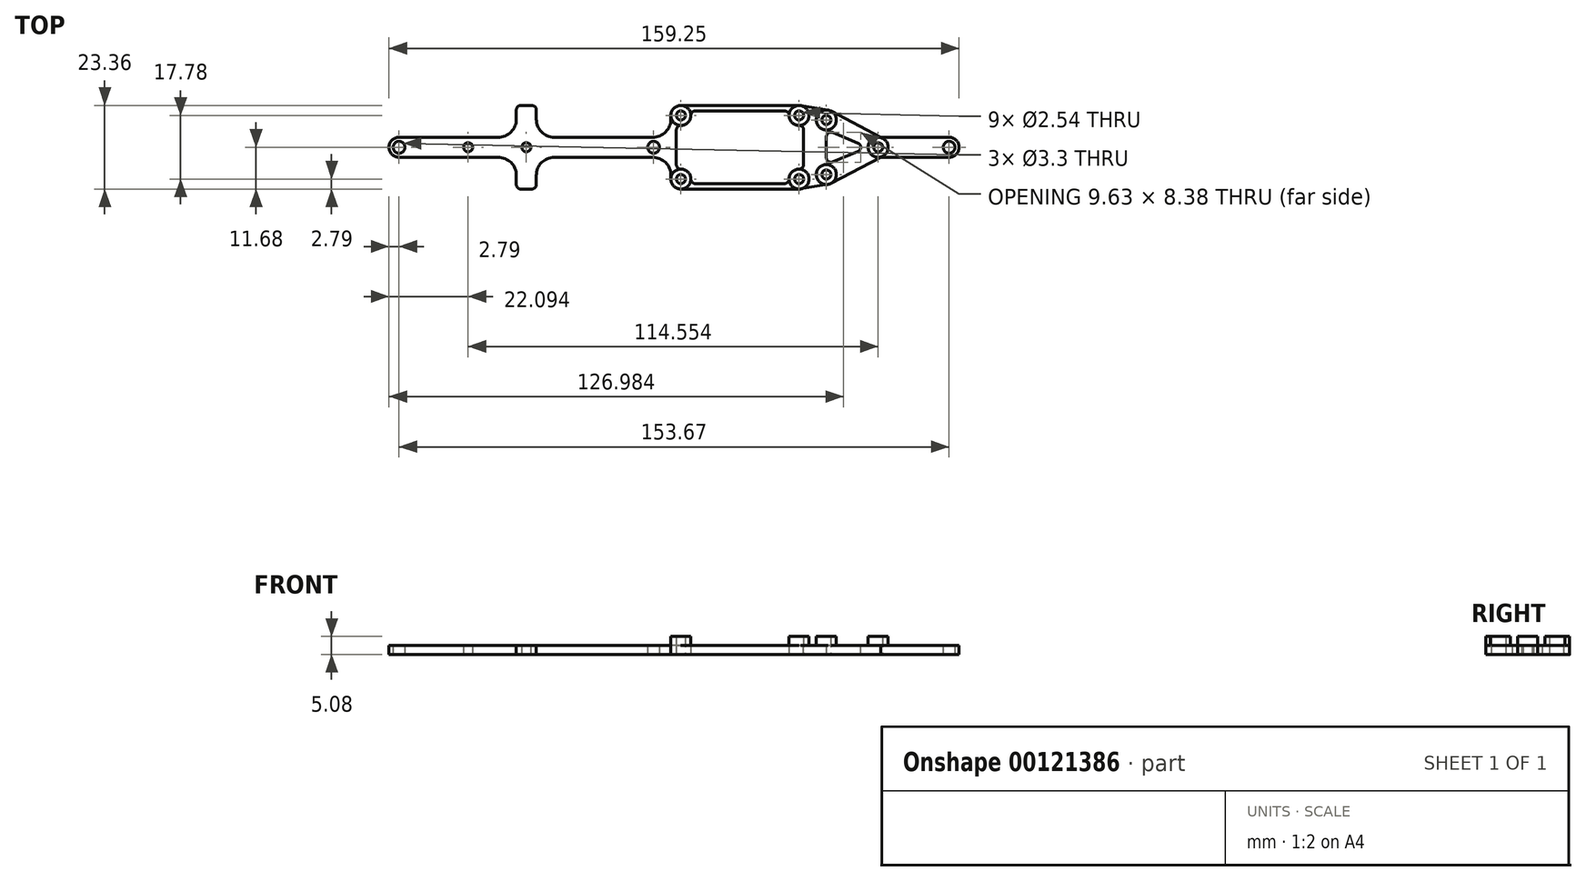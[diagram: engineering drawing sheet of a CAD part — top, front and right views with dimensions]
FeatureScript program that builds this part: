
annotation { "Feature Type Name" : "Feature", "Feature Type Description" : "" }
export const myFeature = defineFeature(function(context is Context, id is Id, definition is map)
    precondition{}
    {
        {
            var Q0;
            Q0=qCreatedBy(makeId("Top.planeOp"),FACE);
            var sketch = newSketch(context, id + "F0", { "sketchPlane" : qUnion([Q0])});
            skCircle(sketch, "E0", {"center": v(-16.51, 8.89) * mm, "radius": 1.27 * mm});
            skCircle(sketch, "E1", {"center": v(-16.51, -8.89) * mm, "radius": 1.27 * mm});
            skCircle(sketch, "E2", {"center": v(16.51, -8.89) * mm, "radius": 1.27 * mm});
            skCircle(sketch, "E3", {"center": v(16.51, 8.89) * mm, "radius": 1.27 * mm});
            skLineSegment(sketch, "E4", {"start": v(-16.51, 8.89) * mm, "end": v(16.51, 8.9) * mm, "construction": true});
            skLineSegment(sketch, "E5", {"start": v(-16.51, 8.89) * mm, "end": v(-16.51, -8.89) * mm, "construction": true});
            skPoint(sketch, "E6", {"position": v(0, 8.9) * mm});
            skPoint(sketch, "E7", {"position": v(-16.51, 0) * mm});
            skCircle(sketch, "E8", {"center": v(24.13, -7.62) * mm, "radius": 1.27 * mm});
            skCircle(sketch, "E9", {"center": v(24.13, 7.62) * mm, "radius": 1.27 * mm});
            skCircle(sketch, "E10", {"center": v(38.6, 0) * mm, "radius": 1.27 * mm});
            skLineSegment(sketch, "E11", {"start": v(25.4, 7.62) * mm, "end": v(25.4, -7.62) * mm, "construction": true});
            skPoint(sketch, "E12", {"position": v(25.4, 0) * mm});
            skCircle(sketch, "E13", {"center": v(-59.69, 0) * mm, "radius": 1.27 * mm});
            skCircle(sketch, "E14", {"center": v(-24.13, 0) * mm, "radius": 1.27 * mm});
            skCircle(sketch, "E15", {"center": v(-95.25, 0) * mm, "radius": 1.65 * mm});
            skCircle(sketch, "E16", {"center": v(58.42, 0) * mm, "radius": 1.65 * mm});
            skCircle(sketch, "E17", {"center": v(-75.95, 0) * mm, "radius": 1.27 * mm});
            skSolve(sketch);
        }
        {
            var Q0;
            Q0=qCreatedBy(makeId("Top.planeOp"),FACE);
            var sketch = newSketch(context, id + "F1", { "sketchPlane" : qUnion([Q0])});
            skCircle(sketch, "E18", {"center": v(-16.51, 8.89) * mm, "radius": 2.8 * mm, "construction": true});
            skCircle(sketch, "E19", {"center": v(-16.51, -8.89) * mm, "radius": 2.8 * mm, "construction": true});
            skCircle(sketch, "E20", {"center": v(16.51, -8.89) * mm, "radius": 2.8 * mm, "construction": true});
            skCircle(sketch, "E21", {"center": v(16.51, 8.9) * mm, "radius": 2.8 * mm, "construction": true});
            skLineSegment(sketch, "E22", {"start": v(-19.3, 8.9) * mm, "end": v(-19.3, 2.8) * mm});
            skLineSegment(sketch, "E23", {"start": v(-16.51, 11.68) * mm, "end": v(16.51, 11.68) * mm});
            skArc(sketch, "E24", {"start": v(-16.51, 11.68) * mm, "mid": v(-18.49, 10.87) * mm, "end": v(-19.3, 8.9) * mm});
            skArc(sketch, "E25", {"start": v(-19.3, -8.89) * mm, "mid": v(-18.49, -10.87) * mm, "end": v(-16.51, -11.68) * mm});
            skArc(sketch, "E26", {"start": v(16.97, 11.65) * mm, "mid": v(16.74, 11.67) * mm, "end": v(16.51, 11.68) * mm});
            skLineSegment(sketch, "E27", {"start": v(-17.78, 6.4) * mm, "end": v(-17.78, -6.4) * mm});
            skLineSegment(sketch, "E28", {"start": v(-14.02, -10.16) * mm, "end": v(14.02, -10.16) * mm});
            skLineSegment(sketch, "E29", {"start": v(17.78, 6.4) * mm, "end": v(17.78, -6.4) * mm});
            skLineSegment(sketch, "E30", {"start": v(-14.02, 10.16) * mm, "end": v(14.02, 10.16) * mm});
            skArc(sketch, "E31", {"start": v(-17.78, 6.4) * mm, "mid": v(-14.53, 6.91) * mm, "end": v(-14.02, 10.16) * mm});
            skArc(sketch, "E32", {"start": v(-14.02, -10.16) * mm, "mid": v(-14.53, -6.91) * mm, "end": v(-17.78, -6.4) * mm});
            skArc(sketch, "E33", {"start": v(14.02, 10.16) * mm, "mid": v(14.53, 6.91) * mm, "end": v(17.78, 6.4) * mm});
            skArc(sketch, "E34", {"start": v(17.78, -6.4) * mm, "mid": v(14.53, -6.91) * mm, "end": v(14.02, -10.16) * mm});
            skCircle(sketch, "E35", {"center": v(-16.51, 8.89) * mm, "radius": 1.27 * mm});
            skCircle(sketch, "E36", {"center": v(16.51, 8.9) * mm, "radius": 1.27 * mm});
            skCircle(sketch, "E37", {"center": v(-16.51, -8.89) * mm, "radius": 1.27 * mm});
            skCircle(sketch, "E38", {"center": v(16.51, -8.89) * mm, "radius": 1.27 * mm});
            skLineSegment(sketch, "E39", {"start": v(16.51, -11.68) * mm, "end": v(-16.51, -11.68) * mm});
            skArc(sketch, "E40", {"start": v(16.51, -11.68) * mm, "mid": v(16.74, -11.67) * mm, "end": v(16.97, -11.65) * mm});
            skCircle(sketch, "E41", {"center": v(24.13, 7.62) * mm, "radius": 2.8 * mm, "construction": true});
            skCircle(sketch, "E42", {"center": v(24.13, -7.62) * mm, "radius": 2.8 * mm, "construction": true});
            skLineSegment(sketch, "E43", {"start": v(16.97, 11.65) * mm, "end": v(24.59, 10.38) * mm});
            skLineSegment(sketch, "E44", {"start": v(16.97, -11.65) * mm, "end": v(24.59, -10.38) * mm});
            skLineSegment(sketch, "E45", {"start": v(39.9, 2.47) * mm, "end": v(39.3, 2.8) * mm, "construction": true});
            skLineSegment(sketch, "E46", {"start": v(25.43, -10.1) * mm, "end": v(39.3, -2.8) * mm});
            skArc(sketch, "E47", {"start": v(25.43, 10.1) * mm, "mid": v(25.02, 10.27) * mm, "end": v(24.59, 10.38) * mm});
            skArc(sketch, "E48", {"start": v(24.59, -10.38) * mm, "mid": v(25.02, -10.27) * mm, "end": v(25.43, -10.1) * mm});
            skCircle(sketch, "E49", {"center": v(38.6, 0) * mm, "radius": 2.8 * mm, "construction": true});
            skLineSegment(sketch, "E50", {"start": v(24.13, 4.83) * mm, "end": v(24.13, -4.83) * mm});
            skLineSegment(sketch, "E51", {"start": v(24.13, -4.83) * mm, "end": v(35.81, 0) * mm});
            skLineSegment(sketch, "E52", {"start": v(35.81, 0) * mm, "end": v(24.13, 4.83) * mm});
            skCircle(sketch, "E53", {"center": v(24.13, 7.62) * mm, "radius": 1.27 * mm});
            skCircle(sketch, "E54", {"center": v(24.13, -7.62) * mm, "radius": 1.27 * mm});
            skCircle(sketch, "E55", {"center": v(38.6, 0) * mm, "radius": 1.27 * mm});
            skLineSegment(sketch, "E56", {"start": v(-62.48, 11.68) * mm, "end": v(-62.48, 2.8) * mm});
            skCircle(sketch, "E57", {"center": v(-59.69, 0) * mm, "radius": 2.8 * mm, "construction": true});
            skPoint(sketch, "E58", {"position": v(-62.48, 0) * mm});
            skLineSegment(sketch, "E59", {"start": v(-19.3, 2.8) * mm, "end": v(-19.3, -2.8) * mm, "construction": true});
            skLineSegment(sketch, "E60", {"start": v(-19.3, -2.8) * mm, "end": v(-19.3, -8.89) * mm});
            skCircle(sketch, "E61", {"center": v(-24.13, 0) * mm, "radius": 2.8 * mm, "construction": true});
            skLineSegment(sketch, "E62", {"start": v(-24.13, 2.8) * mm, "end": v(-19.3, 2.8) * mm});
            skLineSegment(sketch, "E63", {"start": v(-19.3, -2.8) * mm, "end": v(-24.13, -2.8) * mm});
            skLineSegment(sketch, "E64", {"start": v(-62.48, 11.68) * mm, "end": v(-56.9, 11.68) * mm});
            skLineSegment(sketch, "E65", {"start": v(-56.9, 11.68) * mm, "end": v(-56.9, 2.8) * mm});
            skLineSegment(sketch, "E66", {"start": v(-56.9, 2.8) * mm, "end": v(-24.13, 2.8) * mm});
            skLineSegment(sketch, "E67", {"start": v(-24.13, -2.8) * mm, "end": v(-56.9, -2.8) * mm});
            skLineSegment(sketch, "E68", {"start": v(-56.9, -2.8) * mm, "end": v(-56.9, -11.68) * mm});
            skLineSegment(sketch, "E69", {"start": v(-56.9, -11.68) * mm, "end": v(-62.48, -11.68) * mm});
            skCircle(sketch, "E70", {"center": v(-59.69, 0) * mm, "radius": 1.27 * mm});
            skCircle(sketch, "E71", {"center": v(-24.13, 0) * mm, "radius": 1.65 * mm});
            skLineSegment(sketch, "E72", {"start": v(-62.48, 2.8) * mm, "end": v(-62.48, -2.8) * mm, "construction": true});
            skLineSegment(sketch, "E73", {"start": v(-62.48, -2.8) * mm, "end": v(-62.48, -11.68) * mm});
            skLineSegment(sketch, "E74", {"start": v(-62.48, 2.8) * mm, "end": v(-95.25, 2.8) * mm});
            skLineSegment(sketch, "E75", {"start": v(-62.48, -2.8) * mm, "end": v(-95.25, -2.8) * mm});
            skArc(sketch, "E76", {"start": v(-95.25, 2.8) * mm, "mid": v(-98.04, 0) * mm, "end": v(-95.25, -2.8) * mm});
            skCircle(sketch, "E77", {"center": v(-95.25, 0) * mm, "radius": 1.65 * mm});
            skCircle(sketch, "E78", {"center": v(-75.95, 0) * mm, "radius": 1.27 * mm});
            skLineSegment(sketch, "E79", {"start": v(58.42, 2.8) * mm, "end": v(39.3, 2.8) * mm});
            skLineSegment(sketch, "E80", {"start": v(39.3, -2.8) * mm, "end": v(58.42, -2.8) * mm});
            skLineSegment(sketch, "E81", {"start": v(39.3, -2.8) * mm, "end": v(39.9, -2.47) * mm, "construction": true});
            skLineSegment(sketch, "E82", {"start": v(39.3, 2.8) * mm, "end": v(25.43, 10.1) * mm});
            skArc(sketch, "E83", {"start": v(58.42, -2.8) * mm, "mid": v(61.21, 0) * mm, "end": v(58.42, 2.8) * mm});
            skCircle(sketch, "E84", {"center": v(58.42, 0) * mm, "radius": 1.65 * mm});
            skSolve(sketch);
        }
        {
            var Q0;
            Q0 = qSketchRegion(id + "F1", true);
            extrude(context, id + "F2", {"entities" : qUnion([Q0]), "depth" : 2.54 * mm});
        }
        {
            var Q0;
            Q0=makeQuery(id+"F2.opExtrude","CAP_FACE",FACE,{"disambiguationData":[OSD([sQuery(id+"F1.wireOp",EDGE,"E22"),sQuery(id+"F1.wireOp",EDGE,"uU1VLZtT-YTbr-JLfI-A6KJ-TvgWQ5I7Jzmh"),sQuery(id+"F1.wireOp",EDGE,"BFqHJ8J3-t4Px-gx72-p9IC-RT5ytfQASnDa"),sQuery(id+"F1.wireOp",EDGE,"s8fgylly-dl4U-a3sL-DDLo-8xyVy6grNQ6l"),sQuery(id+"F1.wireOp",EDGE,"E23"),sQuery(id+"F1.wireOp",EDGE,"E24"),sQuery(id+"F1.wireOp",EDGE,"E25"),sQuery(id+"F1.wireOp",EDGE,"fYzxbMnw-WgyW-gvi9-hJat-fGDrqmRBlYQs"),sQuery(id+"F1.wireOp",EDGE,"E26"),sQuery(id+"F1.wireOp",EDGE,"Ky7d4IoZ-McTF-fWjv-TmR4-XnRvRbUroFJv"),sQuery(id+"F1.wireOp",EDGE,"E27"),sQuery(id+"F1.wireOp",EDGE,"E28"),sQuery(id+"F1.wireOp",EDGE,"E29"),sQuery(id+"F1.wireOp",EDGE,"E30"),sQuery(id+"F1.wireOp",EDGE,"E31"),sQuery(id+"F1.wireOp",EDGE,"E32"),sQuery(id+"F1.wireOp",EDGE,"E33"),sQuery(id+"F1.wireOp",EDGE,"E34"),sQuery(id+"F1.wireOp",EDGE,"ndVj4wjS-n4GE-cHWh-jopz-p7F9S6QKiJt8"),sQuery(id+"F1.wireOp",EDGE,"fq1kqRq4-wZir-1rh4-uDx0-VhAxuvK0OE4n"),sQuery(id+"F1.wireOp",EDGE,"iL4FsfaZ-fhK5-l9eA-tWqF-QId1HgIxB3gc"),sQuery(id+"F1.wireOp",EDGE,"7jNQX0MP-qTxV-kdyf-NuD0-9IdqTHyKGLDb"),sQuery(id+"F1.wireOp",EDGE,"jRWLSrEc-62Yx-Z2aP-pDAu-Uag0t6lhuvGs"),sQuery(id+"F1.wireOp",EDGE,"Ms8KA7p1-oRK1-IKmq-tgEX-GcjXLNvds0l2"),sQuery(id+"F1.wireOp",EDGE,"E35"),sQuery(id+"F1.wireOp",EDGE,"E36"),sQuery(id+"F1.wireOp",EDGE,"E37"),sQuery(id+"F1.wireOp",EDGE,"E38"),sQuery(id+"F1.wireOp",EDGE,"xTzcSUSB-5c42-cqzY-LloV-dWTL692k8roB"),sQuery(id+"F1.wireOp",EDGE,"mwQopTKn-S8Ts-bFl7-52zz-VJjuvxnOSR3P"),sQuery(id+"F1.wireOp",EDGE,"vEq7pU1P-hbhn-jGhQ-DpaL-gNeL0JwNSjUh")])],"isStart":false});
            var sketch = newSketch(context, id + "F3", { "sketchPlane" : qUnion([Q0])});
            skCircle(sketch, "E85", {"center": v(-16.51, 8.89) * mm, "radius": 2.8 * mm});
            skCircle(sketch, "E86", {"center": v(-16.51, -8.89) * mm, "radius": 2.8 * mm});
            skCircle(sketch, "E87", {"center": v(16.51, 8.9) * mm, "radius": 2.8 * mm});
            skCircle(sketch, "E88", {"center": v(16.51, -8.89) * mm, "radius": 2.8 * mm});
            skCircle(sketch, "E89", {"center": v(24.13, 7.62) * mm, "radius": 2.8 * mm});
            skCircle(sketch, "E90", {"center": v(24.13, -7.62) * mm, "radius": 2.8 * mm});
            skCircle(sketch, "E91", {"center": v(38.6, 0) * mm, "radius": 2.8 * mm});
            skCircle(sketch, "E92", {"center": v(-16.51, 8.89) * mm, "radius": 1.27 * mm});
            skCircle(sketch, "E93", {"center": v(-16.51, -8.89) * mm, "radius": 1.27 * mm});
            skCircle(sketch, "E94", {"center": v(16.51, 8.89) * mm, "radius": 1.27 * mm});
            skCircle(sketch, "E95", {"center": v(24.13, 7.62) * mm, "radius": 1.27 * mm});
            skCircle(sketch, "E96", {"center": v(38.6, 0) * mm, "radius": 1.27 * mm});
            skCircle(sketch, "E97", {"center": v(24.13, -7.62) * mm, "radius": 1.27 * mm});
            skCircle(sketch, "E98", {"center": v(16.51, -8.89) * mm, "radius": 1.27 * mm});
            skSolve(sketch);
        }
        {
            var Q0;
            Q0 = qSketchRegion(id + "F3", true);
            extrude(context, id + "F4", {"entities" : qUnion([Q0]), "operationType" : NewBodyOperationType.ADD, "depth" : 2.54 * mm});
        }
        {
            var Q0;
            Q0=makeQuery(id+"F2.opExtrude","SWEPT_EDGE",EDGE,{"disambiguationData":[OSD([sQuery(id+"F1.wireOp",EDGE,"E56"),sQuery(id+"F1.wireOp",EDGE,"E64")])]});
            var Q1;
            Q1=makeQuery(id+"F2.opExtrude","SWEPT_EDGE",EDGE,{"disambiguationData":[OSD([sQuery(id+"F1.wireOp",EDGE,"E68"),sQuery(id+"F1.wireOp",EDGE,"E69")])]});
            var Q2;
            Q2=makeQuery(id+"F2.opExtrude","SWEPT_EDGE",EDGE,{"disambiguationData":[OSD([sQuery(id+"F1.wireOp",EDGE,"E69"),sQuery(id+"F1.wireOp",EDGE,"E73")])]});
            var Q3;
            Q3=makeQuery(id+"F2.opExtrude","SWEPT_EDGE",EDGE,{"disambiguationData":[OSD([sQuery(id+"F1.wireOp",EDGE,"E30"),sQuery(id+"F1.wireOp",EDGE,"E33")])]});
            var Q4;
            Q4=makeQuery(id+"F2.opExtrude","SWEPT_EDGE",EDGE,{"disambiguationData":[OSD([sQuery(id+"F1.wireOp",EDGE,"E27"),sQuery(id+"F1.wireOp",EDGE,"E31")])]});
            var Q5;
            Q5=makeQuery(id+"F2.opExtrude","SWEPT_EDGE",EDGE,{"disambiguationData":[OSD([sQuery(id+"F1.wireOp",EDGE,"E30"),sQuery(id+"F1.wireOp",EDGE,"E31")])]});
            var Q6;
            Q6=makeQuery(id+"F2.opExtrude","SWEPT_EDGE",EDGE,{"disambiguationData":[OSD([sQuery(id+"F1.wireOp",EDGE,"E28"),sQuery(id+"F1.wireOp",EDGE,"E32")])]});
            var Q7;
            Q7=makeQuery(id+"F2.opExtrude","SWEPT_EDGE",EDGE,{"disambiguationData":[OSD([sQuery(id+"F1.wireOp",EDGE,"E27"),sQuery(id+"F1.wireOp",EDGE,"E32")])]});
            var Q8;
            Q8=makeQuery(id+"F2.opExtrude","SWEPT_EDGE",EDGE,{"disambiguationData":[OSD([sQuery(id+"F1.wireOp",EDGE,"E28"),sQuery(id+"F1.wireOp",EDGE,"E34")])]});
            var Q9;
            Q9=makeQuery(id+"F2.opExtrude","SWEPT_EDGE",EDGE,{"disambiguationData":[OSD([sQuery(id+"F1.wireOp",EDGE,"E29"),sQuery(id+"F1.wireOp",EDGE,"E34")])]});
            var Q10;
            Q10=makeQuery(id+"F2.opExtrude","SWEPT_EDGE",EDGE,{"disambiguationData":[OSD([sQuery(id+"F1.wireOp",EDGE,"E29"),sQuery(id+"F1.wireOp",EDGE,"E33")])]});
            var Q11;
            Q11=makeQuery(id+"F2.opExtrude","SWEPT_EDGE",EDGE,{"disambiguationData":[OSD([sQuery(id+"F1.wireOp",EDGE,"E64"),sQuery(id+"F1.wireOp",EDGE,"E65")])]});
            var Q12;
            Q12=makeQuery(id+"F2.opExtrude","SWEPT_EDGE",EDGE,{"disambiguationData":[OSD([sQuery(id+"F1.wireOp",EDGE,"E68"),sQuery(id+"F1.wireOp",EDGE,"E69")])]});
            var Q13;
            Q13=makeQuery(id+"F2.opExtrude","SWEPT_EDGE",EDGE,{"disambiguationData":[OSD([sQuery(id+"F1.wireOp",EDGE,"E56"),sQuery(id+"F1.wireOp",EDGE,"E64")])]});
            var Q14;
            Q14=makeQuery(id+"F2.opExtrude","SWEPT_EDGE",EDGE,{"disambiguationData":[OSD([sQuery(id+"F1.wireOp",EDGE,"E50"),sQuery(id+"F1.wireOp",EDGE,"E52")])]});
            var Q15;
            Q15=makeQuery(id+"F2.opExtrude","SWEPT_EDGE",EDGE,{"disambiguationData":[OSD([sQuery(id+"F1.wireOp",EDGE,"E50"),sQuery(id+"F1.wireOp",EDGE,"E51")])]});
            var Q16;
            Q16=makeQuery(id+"F2.opExtrude","SWEPT_EDGE",EDGE,{"disambiguationData":[OSD([sQuery(id+"F1.wireOp",EDGE,"E51"),sQuery(id+"F1.wireOp",EDGE,"E52")])]});
            fillet(context, id + "F5", {"entities" : qUnion([Q0, Q1, Q2, Q3, Q4, Q5, Q6, Q7, Q8, Q9, Q10, Q11, Q12, Q13, Q14, Q15, Q16]), "radius" : 1.27 * mm, "tangentPropagation" : true, "allowEdgeOverflow" : false});
        }
        {
            var Q0;
            Q0=makeQuery(id+"F2.opExtrude","SWEPT_EDGE",EDGE,{"disambiguationData":[OSD([sQuery(id+"F1.wireOp",EDGE,"E56"),sQuery(id+"F1.wireOp",EDGE,"E74")])]});
            var Q1;
            Q1=makeQuery(id+"F2.opExtrude","SWEPT_EDGE",EDGE,{"disambiguationData":[OSD([sQuery(id+"F1.wireOp",EDGE,"E22"),sQuery(id+"F1.wireOp",EDGE,"E62")])]});
            var Q2;
            Q2=makeQuery(id+"F2.opExtrude","SWEPT_EDGE",EDGE,{"disambiguationData":[OSD([sQuery(id+"F1.wireOp",EDGE,"E73"),sQuery(id+"F1.wireOp",EDGE,"E75")])]});
            var Q3;
            Q3=makeQuery(id+"F2.opExtrude","SWEPT_EDGE",EDGE,{"disambiguationData":[OSD([sQuery(id+"F1.wireOp",EDGE,"E67"),sQuery(id+"F1.wireOp",EDGE,"E68")])]});
            var Q4;
            Q4=makeQuery(id+"F2.opExtrude","SWEPT_EDGE",EDGE,{"disambiguationData":[OSD([sQuery(id+"F1.wireOp",EDGE,"E65"),sQuery(id+"F1.wireOp",EDGE,"E66")])]});
            var Q5;
            Q5=makeQuery(id+"F2.opExtrude","SWEPT_EDGE",EDGE,{"disambiguationData":[OSD([sQuery(id+"F1.wireOp",EDGE,"E60"),sQuery(id+"F1.wireOp",EDGE,"E63")])]});
            fillet(context, id + "F6", {"entities" : qUnion([Q0, Q1, Q2, Q3, Q4, Q5]), "radius" : 5.08 * mm, "tangentPropagation" : true, "allowEdgeOverflow" : false});
        }
    });
